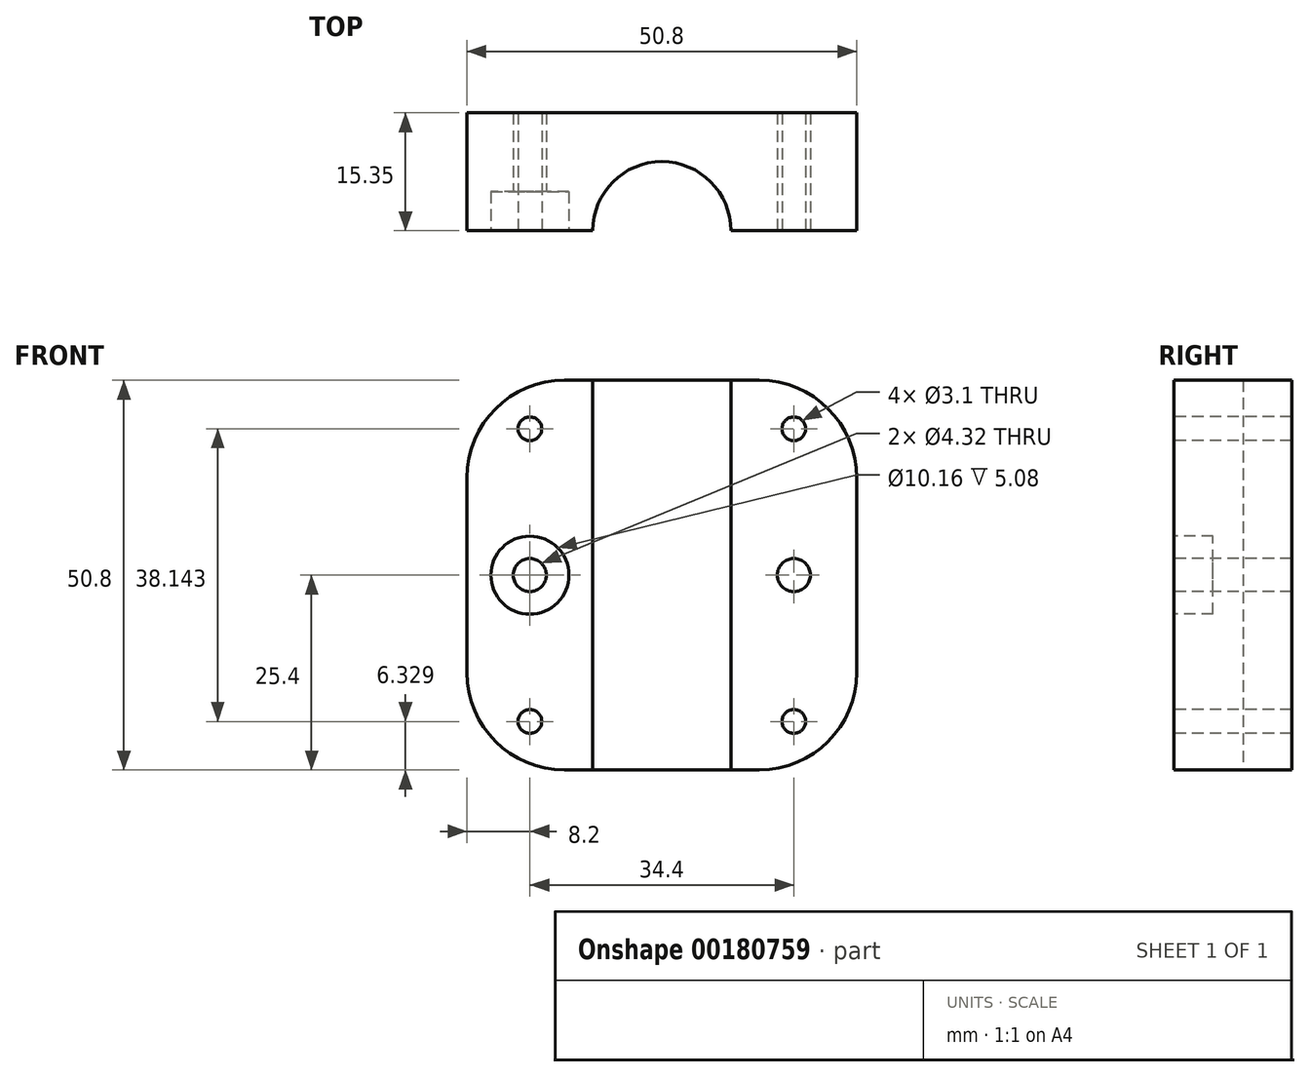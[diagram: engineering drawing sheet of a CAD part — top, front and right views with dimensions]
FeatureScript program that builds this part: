
annotation { "Feature Type Name" : "Feature", "Feature Type Description" : "" }
export const myFeature = defineFeature(function(context is Context, id is Id, definition is map)
    precondition{}
    {
        {
            var Q0;
            Q0=qCreatedBy(makeId("Top.planeOp"),FACE);
            var sketch = newSketch(context, id + "F0", { "sketchPlane" : qUnion([Q0])});
            skLineSegment(sketch, "E0.bottom", {"start": v(25.4, -25.4) * mm, "end": v(-25.4, -25.4) * mm});
            skLineSegment(sketch, "E0.top", {"start": v(25.4, 25.4) * mm, "end": v(-25.4, 25.4) * mm});
            skLineSegment(sketch, "E0.left", {"start": v(25.4, -25.4) * mm, "end": v(25.4, 25.4) * mm});
            skLineSegment(sketch, "E0.right", {"start": v(-25.4, -25.4) * mm, "end": v(-25.4, 25.4) * mm});
            skPoint(sketch, "E0.middle", {"position": v(0, 0) * mm});
            skSolve(sketch);
        }
        {
            var Q0;
            Q0=makeQuery(id+"F0.imprint","IMPRINT",FACE,{"disambiguationData":[TD([[makeQuery(id+"F0.imprint","IMPRINT",EDGE,{"derivedFrom":sQuery(id+"F0.wireOp",EDGE,"E0.bottom")}),-1.0]])]});
            extrude(context, id + "F1", {"entities" : qUnion([Q0]), "depth" : 50.8 * mm});
        }
        {
            var Q0;
            Q0=makeQuery(id+"F1.opExtrude","CAP_FACE",FACE,{"disambiguationData":[OSD([sQuery(id+"F0.wireOp",EDGE,"E0.bottom"),sQuery(id+"F0.wireOp",EDGE,"E0.top"),sQuery(id+"F0.wireOp",EDGE,"E0.left"),sQuery(id+"F0.wireOp",EDGE,"E0.right")])],"isStart":true});
            var sketch = newSketch(context, id + "F2", { "sketchPlane" : qUnion([Q0])});
            skCircle(sketch, "E1", {"center": v(0, 0) * mm, "radius": 9 * mm});
            skSolve(sketch);
        }
        {
            var Q0;
            Q0=qSketchRegion(id+"F2",true);
            extrude(context, id + "F3", {"entities" : qUnion([Q0]), "operationType" : NewBodyOperationType.REMOVE, "oppositeDirection" : true, "depth" : 407.42 * mm});
        }
        {
            var Q0;
            Q0=makeQuery(id+"F1.opExtrude","CAP_FACE",FACE,{"disambiguationData":[OSD([sQuery(id+"F0.wireOp",EDGE,"E0.bottom"),sQuery(id+"F0.wireOp",EDGE,"E0.top"),sQuery(id+"F0.wireOp",EDGE,"E0.left"),sQuery(id+"F0.wireOp",EDGE,"E0.right")])],"isStart":true});
            var sketch = newSketch(context, id + "F4", { "sketchPlane" : qUnion([Q0])});
            skLineSegment(sketch, "E2.bottom", {"start": v(-25.4, 25.4) * mm, "end": v(34.72, 25.4) * mm});
            skLineSegment(sketch, "E2.top", {"start": v(-25.4, 0) * mm, "end": v(34.72, 0) * mm});
            skLineSegment(sketch, "E2.left", {"start": v(-25.4, 25.4) * mm, "end": v(-25.4, 0) * mm});
            skLineSegment(sketch, "E2.right", {"start": v(34.72, 25.4) * mm, "end": v(34.72, 0) * mm});
            skSolve(sketch);
        }
        {
            var Q0;
            Q0=qSketchRegion(id+"F4",true);
            extrude(context, id + "F5", {"entities" : qUnion([Q0]), "operationType" : NewBodyOperationType.REMOVE, "oppositeDirection" : true, "depth" : 338.58 * mm});
        }
        {
            var Q0;
            {var subQ0=sQuery(id+"F0.wireOp",EDGE,"E0.right");Q0=makeQuery(id+"F5.boolean.opBoolean","COPY",FACE,{"disambiguationData":[TD([makeQuery(id+"F1.opExtrude","SWEPT_FACE",FACE,{"disambiguationData":[OSD([subQ0])]})])],"derivedFrom":makeQuery(id+"F5.opExtrude","SWEPT_FACE",FACE,{"disambiguationData":[OSD([sQuery(id+"F4.wireOp",EDGE,"E2.top")])]})});}
            var sketch = newSketch(context, id + "F6", { "sketchPlane" : qUnion([Q0])});
            skCircle(sketch, "E3", {"center": v(-17.2, 25.4) * mm, "radius": 5.08 * mm});
            skSolve(sketch);
        }
        {
            var Q0;
            Q0=qSketchRegion(id+"F6",true);
            extrude(context, id + "F7", {"entities" : qUnion([Q0]), "operationType" : NewBodyOperationType.REMOVE, "oppositeDirection" : true, "depth" : 5.08 * mm});
        }
        {
            var Q0;
            Q0=makeQuery(id+"F7.boolean.opBoolean","COPY",FACE,{"derivedFrom":makeQuery(id+"F7.opExtrude","CAP_FACE",FACE,{"disambiguationData":[OSD([sQuery(id+"F6.wireOp",EDGE,"E3")])],"isStart":false})});
            var sketch = newSketch(context, id + "F8", { "sketchPlane" : qUnion([Q0])});
            skCircle(sketch, "E4", {"center": v(-17.2, 25.4) * mm, "radius": 2.16 * mm});
            skSolve(sketch);
        }
        {
            var Q0;
            Q0=qSketchRegion(id+"F8",true);
            extrude(context, id + "F9", {"entities" : qUnion([Q0]), "operationType" : NewBodyOperationType.REMOVE, "oppositeDirection" : true, "depth" : 25.4 * mm});
        }
        {
            var Q0;
            {var subQ0=sQuery(id+"F0.wireOp",EDGE,"E0.right");Q0=makeQuery(id+"F5.boolean.opBoolean","COPY",FACE,{"disambiguationData":[TD([makeQuery(id+"F1.opExtrude","SWEPT_FACE",FACE,{"disambiguationData":[OSD([subQ0])]})])],"derivedFrom":makeQuery(id+"F5.opExtrude","SWEPT_FACE",FACE,{"disambiguationData":[OSD([sQuery(id+"F4.wireOp",EDGE,"E2.top")])]})});}
            var sketch = newSketch(context, id + "F10", { "sketchPlane" : qUnion([Q0])});
            skCircle(sketch, "E5", {"center": v(-17.2, 44.47) * mm, "radius": 1.55 * mm});
            skPoint(sketch, "E5.centerSnap0", {"position": v(-17.2, 50.8) * mm});
            skSolve(sketch);
        }
        {
            var Q0;
            Q0=qSketchRegion(id+"F10",true);
            extrude(context, id + "F11", {"entities" : qUnion([Q0]), "operationType" : NewBodyOperationType.REMOVE, "oppositeDirection" : true, "depth" : 25.4 * mm});
        }
        {
            var Q0;
            {var subQ0=sQuery(id+"F0.wireOp",EDGE,"E0.right");Q0=makeQuery(id+"F5.boolean.opBoolean","COPY",FACE,{"disambiguationData":[TD([makeQuery(id+"F1.opExtrude","SWEPT_FACE",FACE,{"disambiguationData":[OSD([subQ0])]})])],"derivedFrom":makeQuery(id+"F5.opExtrude","SWEPT_FACE",FACE,{"disambiguationData":[OSD([sQuery(id+"F4.wireOp",EDGE,"E2.top")])]})});}
            var sketch = newSketch(context, id + "F12", { "sketchPlane" : qUnion([Q0])});
            skCircle(sketch, "E6.MirrorC", {"center": v(17.2, 44.47) * mm, "radius": 1.55 * mm});
            skCircle(sketch, "E7.MirrorC", {"center": v(17.2, 25.4) * mm, "radius": 5.08 * mm, "construction": true});
            skCircle(sketch, "E8.MirrorC", {"center": v(17.2, 25.4) * mm, "radius": 2.16 * mm});
            skSolve(sketch);
        }
        {
            var Q0;
            Q0=qSketchRegion(id+"F12",true);
            extrude(context, id + "F13", {"entities" : qUnion([Q0]), "operationType" : NewBodyOperationType.REMOVE, "oppositeDirection" : true, "depth" : 25.4 * mm});
        }
        {
            var Q0;
            {var subQ1=sQuery(id+"F0.wireOp",EDGE,"E0.left");Q0=makeQuery(id+"F5.boolean.opBoolean","COPY",FACE,{"disambiguationData":[TD([makeQuery(id+"F1.opExtrude","SWEPT_FACE",FACE,{"disambiguationData":[OSD([subQ1])]})])],"derivedFrom":makeQuery(id+"F5.opExtrude","SWEPT_FACE",FACE,{"disambiguationData":[OSD([sQuery(id+"F4.wireOp",EDGE,"E2.top")])]})});}
            var sketch = newSketch(context, id + "F14", { "sketchPlane" : qUnion([Q0])});
            skCircle(sketch, "E9.MirrorC", {"center": v(17.2, 25.4) * mm, "radius": 5.08 * mm});
            skSolve(sketch);
        }
        {
            var Q0;
            Q0=makeQuery(id+"F1.opExtrude","CAP_FACE",FACE,{"disambiguationData":[OSD([sQuery(id+"F0.wireOp",EDGE,"E0.bottom"),sQuery(id+"F0.wireOp",EDGE,"E0.top"),sQuery(id+"F0.wireOp",EDGE,"E0.left"),sQuery(id+"F0.wireOp",EDGE,"E0.right")])],"isStart":false});
            cPlane(context, id + "F15", {"entities" : qUnion([Q0]), "cplaneType" : CPlaneType.OFFSET, "offset" : 25.4 * mm, "oppositeDirection" : true, "width" : 152.4 * mm, "height" : 152.4 * mm});
        }
        {
            var Q0;
            Q0=makeQuery(id+"F1.opExtrude","SWEPT_BODY",BODY,{"disambiguationData":[OSD([sQuery(id+"F0.wireOp",EDGE,"E0.bottom"),sQuery(id+"F0.wireOp",EDGE,"E0.top"),sQuery(id+"F0.wireOp",EDGE,"E0.left"),sQuery(id+"F0.wireOp",EDGE,"E0.right")])]});
            var Q1;
            Q1=qCreatedBy(id+"F15.planeOp",FACE);
            mirror(context, id + "F16", {"operationType" : NewBodyOperationType.INTERSECT, "entities" : qUnion([Q0]), "mirrorPlane" : qUnion([Q1])});
        }
        {
            var Q0;
            Q0=makeQuery(id+"F1.opExtrude","CAP_FACE",FACE,{"disambiguationData":[OSD([sQuery(id+"F0.wireOp",EDGE,"E0.bottom"),sQuery(id+"F0.wireOp",EDGE,"E0.top"),sQuery(id+"F0.wireOp",EDGE,"E0.left"),sQuery(id+"F0.wireOp",EDGE,"E0.right")])],"isStart":true});
            var sketch = newSketch(context, id + "F17", { "sketchPlane" : qUnion([Q0])});
            skLineSegment(sketch, "E10", {"start": v(0, -9) * mm, "end": v(0, -15.35) * mm});
            skLineSegment(sketch, "E11", {"start": v(0, -15.35) * mm, "end": v(-44.71, -15.35) * mm});
            skLineSegment(sketch, "E12", {"start": v(-44.71, -15.35) * mm, "end": v(-42.65, -31.93) * mm});
            skLineSegment(sketch, "E13", {"start": v(-42.65, -31.93) * mm, "end": v(43.38, -33.96) * mm});
            skLineSegment(sketch, "E14", {"start": v(0, -15.35) * mm, "end": v(37.31, -15.35) * mm});
            skLineSegment(sketch, "E15", {"start": v(37.31, -15.35) * mm, "end": v(43.38, -33.96) * mm});
            skSolve(sketch);
        }
        {
            var Q0;
            Q0=qSketchRegion(id+"F17",true);
            extrude(context, id + "F18", {"entities" : qUnion([Q0]), "operationType" : NewBodyOperationType.REMOVE, "oppositeDirection" : true, "depth" : 72.39 * mm});
        }
        {
            var Q0;
            {var subQ0=sQuery(id+"F0.wireOp",EDGE,"E0.right");Q0=makeQuery(id+"F5.boolean.opBoolean","COPY",FACE,{"disambiguationData":[TD([makeQuery(id+"F1.opExtrude","SWEPT_FACE",FACE,{"disambiguationData":[OSD([subQ0])]})])],"derivedFrom":makeQuery(id+"F5.opExtrude","SWEPT_FACE",FACE,{"disambiguationData":[OSD([sQuery(id+"F4.wireOp",EDGE,"E2.top")])]})});}
            var sketch = newSketch(context, id + "F19", { "sketchPlane" : qUnion([Q0])});
            skLineSegment(sketch, "E16.bottom", {"start": v(-21.86, 2.54) * mm, "end": v(-9.9, 2.54) * mm});
            skLineSegment(sketch, "E16.top", {"start": v(-21.86, 48.26) * mm, "end": v(-9.9, 48.26) * mm});
            skLineSegment(sketch, "E16.left", {"start": v(-21.86, 2.54) * mm, "end": v(-21.86, 48.26) * mm});
            skLineSegment(sketch, "E16.right", {"start": v(21.86, 2.54) * mm, "end": v(21.86, 48.26) * mm});
            skPoint(sketch, "E16.middle", {"position": v(0, 25.4) * mm});
            skPoint(sketch, "E16.middle.positionSnap0", {"position": v(-25.4, 25.4) * mm});
            skPoint(sketch, "E16.centerSnap0", {"position": v(-25.4, 25.4) * mm});
            skLineSegment(sketch, "E17.0", {"start": v(-9.9, 48.26) * mm, "end": v(-9.9, 2.54) * mm});
            skLineSegment(sketch, "E18", {"start": v(9.9, 48.26) * mm, "end": v(9.9, 2.54) * mm});
            skLineSegment(sketch, "E19.trimOffspring", {"start": v(9.9, 48.26) * mm, "end": v(21.86, 48.26) * mm});
            skPoint(sketch, "E20.orphan", {"position": v(0, 2.54) * mm});
            skPoint(sketch, "E21.start.orphan", {"position": v(0, 48.26) * mm});
            skLineSegment(sketch, "E22.trimOffspring", {"start": v(9.9, 2.54) * mm, "end": v(21.86, 2.54) * mm});
            skSolve(sketch);
        }
        {
            var Q0;
            {var subQ1=sQuery(id+"F0.wireOp",EDGE,"E0.left");Q0=makeQuery(id+"F5.boolean.opBoolean","COPY",FACE,{"disambiguationData":[TD([makeQuery(id+"F1.opExtrude","SWEPT_FACE",FACE,{"disambiguationData":[OSD([subQ1])]})])],"derivedFrom":makeQuery(id+"F5.opExtrude","SWEPT_FACE",FACE,{"disambiguationData":[OSD([sQuery(id+"F4.wireOp",EDGE,"E2.top")])]})});}
            var sketch = newSketch(context, id + "F20", { "sketchPlane" : qUnion([Q0])});
            skCircle(sketch, "E23.0", {"center": v(-17.2, 44.47) * mm, "radius": 1.55 * mm});
            skCircle(sketch, "E24.0", {"center": v(-17.2, 25.4) * mm, "radius": 5.08 * mm});
            skArc(sketch, "E25", {"start": v(-18.8, 33.22) * mm, "mid": v(-17.18, 17.42) * mm, "end": v(-15.62, 33.23) * mm});
            skLineSegment(sketch, "E26.0", {"start": v(-18.8, 41.9) * mm, "end": v(-18.8, 33.22) * mm});
            skArc(sketch, "E27", {"start": v(-15.62, 41.89) * mm, "mid": v(-17.18, 47.5) * mm, "end": v(-18.8, 41.9) * mm});
            skLineSegment(sketch, "E28.0", {"start": v(-15.62, 41.89) * mm, "end": v(-15.62, 33.23) * mm});
            skLineSegment(sketch, "E29.0", {"start": v(-9, 47.6) * mm, "end": v(-22.2, 47.6) * mm});
            skLineSegment(sketch, "E29.1", {"start": v(-9, 47.6) * mm, "end": v(9, 47.6) * mm});
            skLineSegment(sketch, "E29.2", {"start": v(-22.2, 47.6) * mm, "end": v(-22.2, 3.2) * mm});
            skLineSegment(sketch, "E29.3", {"start": v(22.2, 47.6) * mm, "end": v(9, 47.6) * mm});
            skLineSegment(sketch, "E29.4", {"start": v(-22.2, 3.2) * mm, "end": v(-9, 3.2) * mm});
            skLineSegment(sketch, "E29.5", {"start": v(9, 3.2) * mm, "end": v(-9, 3.2) * mm});
            skLineSegment(sketch, "E29.6", {"start": v(9, 3.2) * mm, "end": v(22.2, 3.2) * mm});
            skLineSegment(sketch, "E29.7", {"start": v(22.2, 47.6) * mm, "end": v(22.2, 3.2) * mm});
            skLineSegment(sketch, "E30", {"start": v(-12.18, 47.6) * mm, "end": v(-12.18, 3.2) * mm});
            skLineSegment(sketch, "E31.0", {"start": v(-9, 50.8) * mm, "end": v(-9, 0) * mm, "construction": true});
            skSolve(sketch);
        }
        {
            var Q0;
            Q0=makeQuery(id+"F1.opExtrude","CAP_EDGE",EDGE,{"disambiguationData":[OSD([sQuery(id+"F0.wireOp",EDGE,"E0.left")])],"isStart":false});
            var Q1;
            Q1=makeQuery(id+"F1.opExtrude","CAP_EDGE",EDGE,{"disambiguationData":[OSD([sQuery(id+"F0.wireOp",EDGE,"E0.left")])],"isStart":true});
            var Q2;
            Q2=makeQuery(id+"F1.opExtrude","CAP_EDGE",EDGE,{"disambiguationData":[OSD([sQuery(id+"F0.wireOp",EDGE,"E0.right")])],"isStart":false});
            var Q3;
            Q3=makeQuery(id+"F1.opExtrude","CAP_EDGE",EDGE,{"disambiguationData":[OSD([sQuery(id+"F0.wireOp",EDGE,"E0.right")])],"isStart":true});
            fillet(context, id + "F21", {"entities" : qUnion([Q0, Q1, Q2, Q3]), "radius" : 12.7 * mm, "tangentPropagation" : true, "allowEdgeOverflow" : false});
        }
    });
